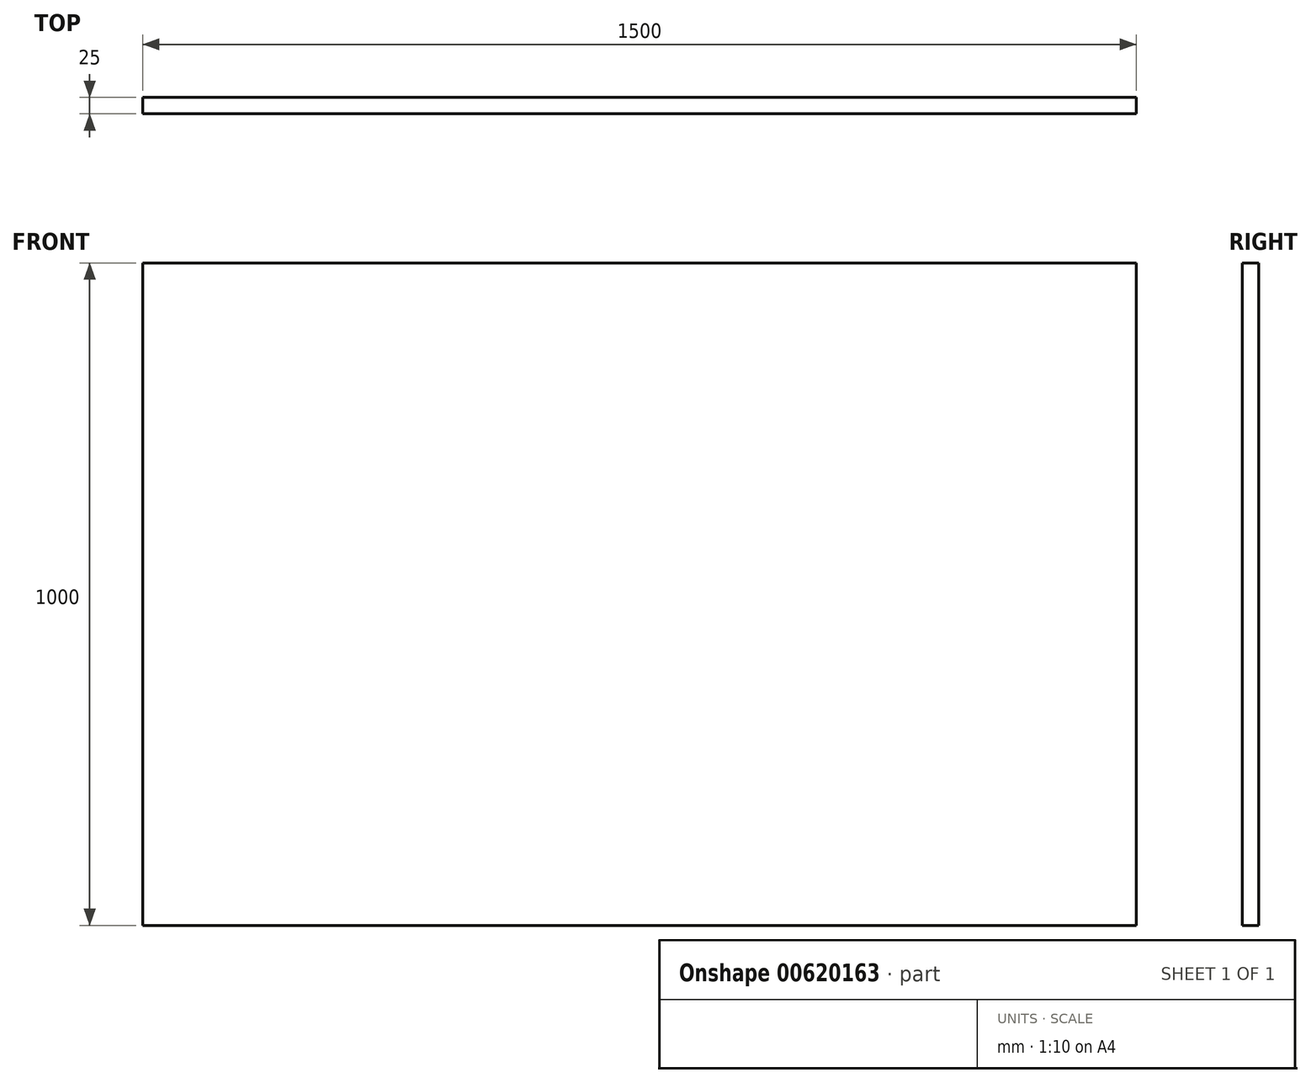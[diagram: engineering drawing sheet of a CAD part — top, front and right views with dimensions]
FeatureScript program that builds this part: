
annotation { "Feature Type Name" : "Feature", "Feature Type Description" : "" }
export const myFeature = defineFeature(function(context is Context, id is Id, definition is map)
    precondition{}
    {
        {
            var Q0;
            Q0=qCreatedBy(makeId("Front.planeOp"),FACE);
            var sketch = newSketch(context, id + "F0", { "sketchPlane" : qUnion([Q0])});
            skLineSegment(sketch, "E0.bottom", {"start": v(-750, 0) * mm, "end": v(750, 0) * mm});
            skLineSegment(sketch, "E0.top", {"start": v(-750, 1000) * mm, "end": v(750, 1000) * mm});
            skLineSegment(sketch, "E0.left", {"start": v(-750, 0) * mm, "end": v(-750, 1000) * mm});
            skLineSegment(sketch, "E0.right", {"start": v(750, 0) * mm, "end": v(750, 1000) * mm});
            skSolve(sketch);
        }
        {
            var Q0;
            Q0=makeQuery(id+"F0.imprint","IMPRINT",FACE,{"disambiguationData":[TD([[makeQuery(id+"F0.imprint","IMPRINT",EDGE,{"derivedFrom":sQuery(id+"F0.wireOp",EDGE,"E0.bottom")}),1.0]])]});
            extrude(context, id + "F1", {"entities" : qUnion([Q0]), "depth" : 25 * mm, "offsetDistance" : 25 * mm});
        }
    });
